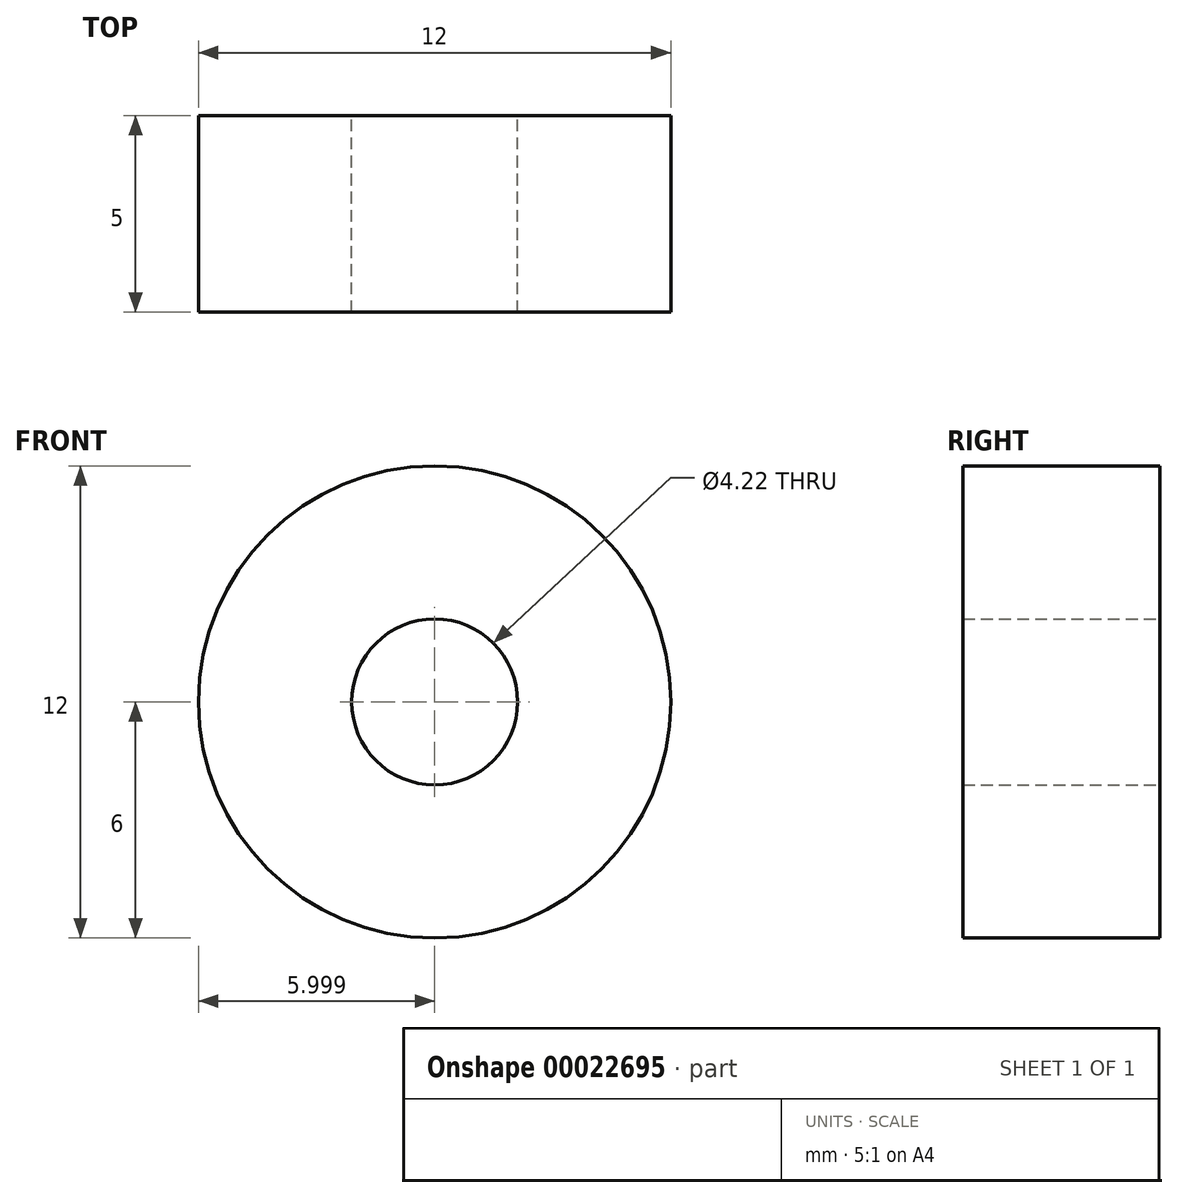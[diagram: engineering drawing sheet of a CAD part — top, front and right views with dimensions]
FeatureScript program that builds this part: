
annotation { "Feature Type Name" : "Feature", "Feature Type Description" : "" }
export const myFeature = defineFeature(function(context is Context, id is Id, definition is map)
    precondition{}
    {
        {
            var Q0;
            Q0=qCreatedBy(makeId("Front.planeOp"),FACE);
            var sketch = newSketch(context, id + "F0", { "sketchPlane" : qUnion([Q0])});
            skCircle(sketch, "E0", {"center": v(-25.53, 2.27) * mm, "radius": 6 * mm});
            skCircle(sketch, "E1", {"center": v(-25.53, 2.27) * mm, "radius": 2.1 * mm});
            skSolve(sketch);
        }
        {
            var Q0;
            Q0=makeQuery(id+"F0.imprint","IMPRINT",FACE,{"disambiguationData":[TD([[makeQuery(id+"F0.imprint","IMPRINT",EDGE,{"derivedFrom":sQuery(id+"F0.wireOp",EDGE,"E0")}),1.0]])]});
            extrude(context, id + "F1", {"entities" : qUnion([Q0]), "endBound" : BoundingType.SYMMETRIC, "depth" : 5 * mm});
        }
    });
